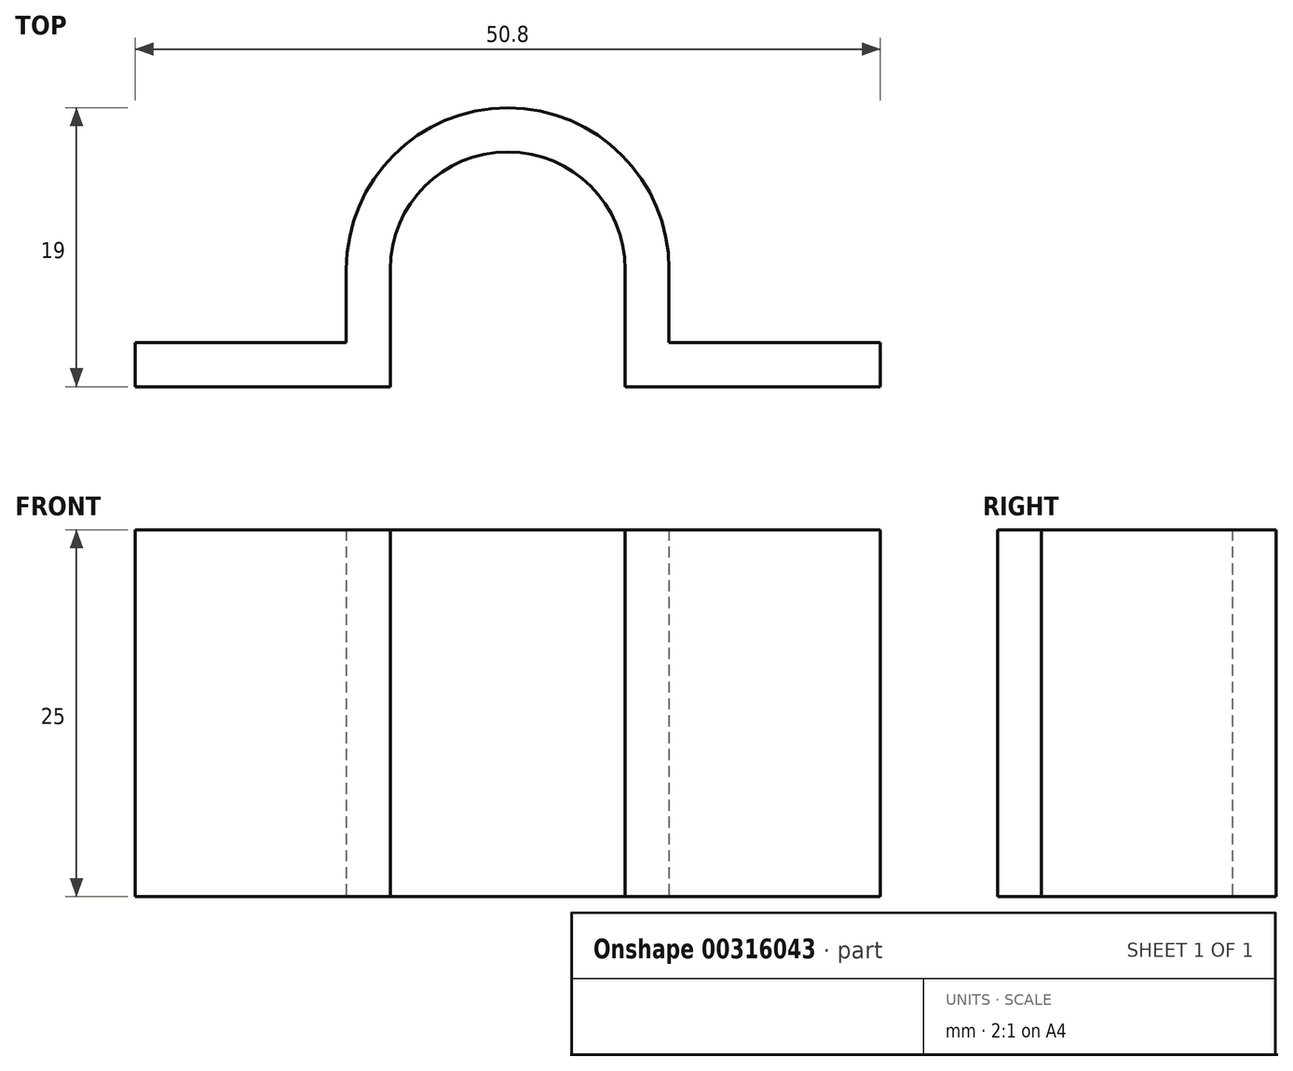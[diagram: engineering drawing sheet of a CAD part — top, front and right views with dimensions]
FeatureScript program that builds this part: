
annotation { "Feature Type Name" : "Feature", "Feature Type Description" : "" }
export const myFeature = defineFeature(function(context is Context, id is Id, definition is map)
    precondition{}
    {
        {
            var Q0;
            Q0=qCreatedBy(makeId("Top.planeOp"),FACE);
            var sketch = newSketch(context, id + "F0", { "sketchPlane" : qUnion([Q0])});
            skCircle(sketch, "E0", {"center": v(0, 8) * mm, "radius": 8 * mm, "construction": true});
            skArc(sketch, "E1", {"start": v(8, 8) * mm, "mid": v(0, 16) * mm, "end": v(-8, 8) * mm});
            skArc(sketch, "E2", {"start": v(11, 8) * mm, "mid": v(0, 19) * mm, "end": v(-11, 8) * mm});
            skLineSegment(sketch, "E3.bottom", {"start": v(25.4, 0) * mm, "end": v(8, 0) * mm});
            skLineSegment(sketch, "E3.top", {"start": v(25.4, 3) * mm, "end": v(11, 3) * mm});
            skLineSegment(sketch, "E3.left", {"start": v(25.4, 0) * mm, "end": v(25.4, 3) * mm});
            skLineSegment(sketch, "E3.right", {"start": v(-25.4, 0) * mm, "end": v(-25.4, 3) * mm});
            skPoint(sketch, "E3.middle", {"position": v(0, 1.5) * mm});
            skLineSegment(sketch, "E4.left", {"start": v(11, 3) * mm, "end": v(11, 8) * mm});
            skLineSegment(sketch, "E4.right", {"start": v(-11, 3) * mm, "end": v(-11, 8) * mm});
            skPoint(sketch, "E4.middle", {"position": v(0, 4) * mm});
            skLineSegment(sketch, "E5.left", {"start": v(8, 0) * mm, "end": v(8, 8) * mm});
            skLineSegment(sketch, "E5.right", {"start": v(-8, 0) * mm, "end": v(-8, 8) * mm});
            skLineSegment(sketch, "E6.trimOffspring", {"start": v(-8, 0) * mm, "end": v(-25.4, 0) * mm});
            skLineSegment(sketch, "E7.trimOffspring", {"start": v(-11, 3) * mm, "end": v(-25.4, 3) * mm});
            skPoint(sketch, "E8.orphan", {"position": v(-11, 0) * mm});
            skPoint(sketch, "E9.orphan", {"position": v(11, 0) * mm});
            skSolve(sketch);
        }
        {
            var Q0;
            Q0 = qSketchRegion(id + "F0", true);
            extrude(context, id + "F1", {"entities" : qUnion([Q0]), "depth" : 25 * mm});
        }
    });
